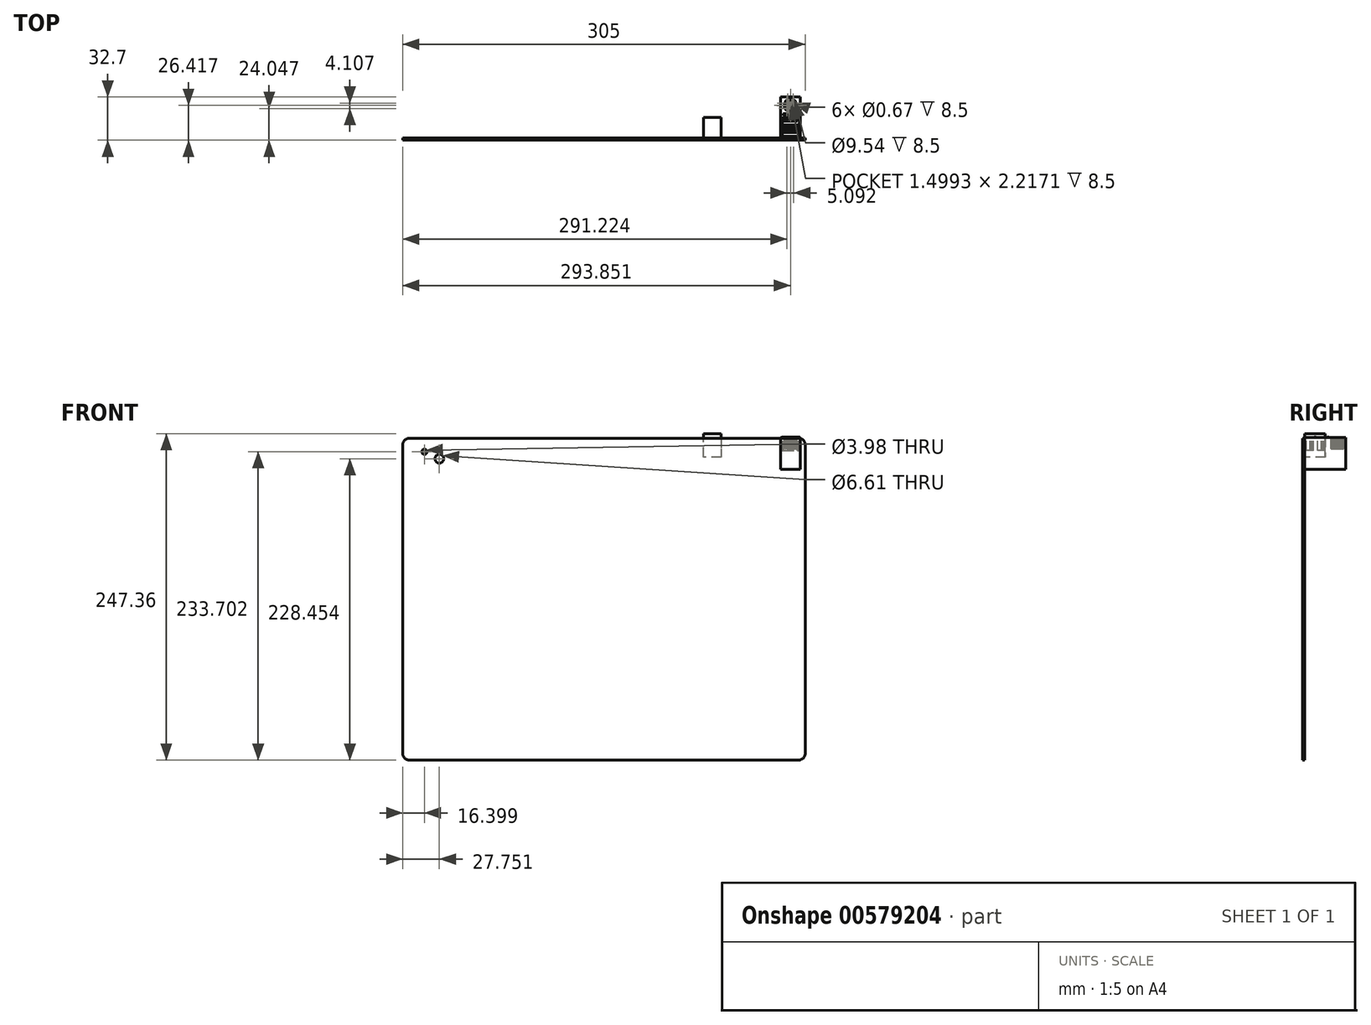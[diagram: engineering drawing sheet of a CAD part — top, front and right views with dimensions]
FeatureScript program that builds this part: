
annotation { "Feature Type Name" : "Feature", "Feature Type Description" : "" }
export const myFeature = defineFeature(function(context is Context, id is Id, definition is map)
    precondition{}
    {
        {
            var Q0;
            Q0=qCreatedBy(makeId("Front.planeOp"),FACE);
            var sketch = newSketch(context, id + "F0", { "sketchPlane" : qUnion([Q0])});
            skPoint(sketch, "E0", {"position": v(-153.4, 107.43) * mm});
            skLineSegment(sketch, "E1", {"start": v(-148.4, 107.43) * mm, "end": v(146.6, 107.43) * mm});
            skPoint(sketch, "E2", {"position": v(151.6, 107.43) * mm});
            skPoint(sketch, "E3", {"position": v(151.6, -136.57) * mm});
            skLineSegment(sketch, "E4", {"start": v(-153.4, 102.43) * mm, "end": v(-153.4, -131.57) * mm});
            skLineSegment(sketch, "E5", {"start": v(-148.4, -136.57) * mm, "end": v(146.6, -136.57) * mm});
            skLineSegment(sketch, "E6", {"start": v(151.6, -131.57) * mm, "end": v(151.6, 102.43) * mm});
            skArc(sketch, "E7.filletArc", {"start": v(-148.4, 107.43) * mm, "mid": v(-151.94, 105.97) * mm, "end": v(-153.4, 102.43) * mm});
            skPoint(sketch, "E8.visualSharp", {"position": v(-153.4, -136.57) * mm});
            skArc(sketch, "E8.filletArc", {"start": v(-153.4, -131.57) * mm, "mid": v(-151.94, -135.1) * mm, "end": v(-148.4, -136.57) * mm});
            skArc(sketch, "E9.filletArc", {"start": v(146.6, -136.57) * mm, "mid": v(150.13, -135.1) * mm, "end": v(151.6, -131.57) * mm});
            skArc(sketch, "E10.filletArc", {"start": v(151.6, 102.43) * mm, "mid": v(150.13, 105.97) * mm, "end": v(146.6, 107.43) * mm});
            skCircle(sketch, "E11", {"center": v(-137, 97.13) * mm, "radius": 1.99 * mm});
            skCircle(sketch, "E12", {"center": v(-125.65, 91.88) * mm, "radius": 3.3 * mm});
            skLineSegment(sketch, "E13.bottom", {"start": v(148.03, 83.7) * mm, "end": v(133.05, 83.7) * mm});
            skLineSegment(sketch, "E13.top", {"start": v(148.03, 108) * mm, "end": v(133.05, 108) * mm});
            skLineSegment(sketch, "E13.left", {"start": v(148.03, 83.7) * mm, "end": v(148.03, 108) * mm});
            skLineSegment(sketch, "E13.right", {"start": v(133.05, 83.7) * mm, "end": v(133.05, 108) * mm});
            skSolve(sketch);
        }
        {
            var Q0;
            {var subQ0=sQuery(id+"F0.wireOp",EDGE,"E13.bottom");Q0=makeQuery(id+"F0.imprint","IMPRINT",FACE,{"disambiguationData":[TD([[makeQuery(id+"F0.imprint","IMPRINT",EDGE,{"derivedFrom":subQ0}),-1.0]])]});}
            var Q1;
            {var subQ1=sQuery(id+"F0.wireOp",EDGE,"E13.top");Q1=makeQuery(id+"F0.imprint","IMPRINT",FACE,{"disambiguationData":[TD([[makeQuery(id+"F0.imprint","IMPRINT",EDGE,{"derivedFrom":subQ1}),1.0]])]});}
            extrude(context, id + "F1", {"entities" : qUnion([Q0, Q1]), "oppositeDirection" : true, "depth" : 31.1 * mm, "offsetDistance" : 25 * mm});
        }
        {
            var Q0;
            Q0=makeQuery(id+"F1.opExtrude","SWEPT_FACE",FACE,{"disambiguationData":[OSD([sQuery(id+"F0.wireOp",EDGE,"E13.top")])]});
            var sketch = newSketch(context, id + "F2", { "sketchPlane" : qUnion([Q0])});
            skCircle(sketch, "E14", {"center": v(140.45, 24.82) * mm, "radius": 4.1 * mm});
            skPoint(sketch, "E14.first.point", {"position": v(137.53, 27.7) * mm});
            skPoint(sketch, "E14.second.point", {"position": v(143.22, 21.78) * mm});
            skPoint(sketch, "E14.third.point", {"position": v(139.8, 20.76) * mm});
            skCircle(sketch, "E15", {"center": v(138.27, 26.54) * mm, "radius": 0.34 * mm});
            skPoint(sketch, "E15.first.point", {"position": v(138.08, 26.81) * mm});
            skPoint(sketch, "E15.second.point", {"position": v(138.5, 26.29) * mm});
            skPoint(sketch, "E15.third.point", {"position": v(138.28, 26.2) * mm});
            skCircle(sketch, "E16", {"center": v(137.82, 24.54) * mm, "radius": 0.34 * mm});
            skPoint(sketch, "E16.first.point", {"position": v(137.63, 24.82) * mm});
            skPoint(sketch, "E16.second.point", {"position": v(138, 24.26) * mm});
            skPoint(sketch, "E16.third.point", {"position": v(137.6, 24.3) * mm});
            skCircle(sketch, "E17", {"center": v(139.37, 22.5) * mm, "radius": 0.34 * mm});
            skPoint(sketch, "E17.first.point", {"position": v(139.18, 22.77) * mm});
            skPoint(sketch, "E17.second.point", {"position": v(139.53, 22.2) * mm});
            skPoint(sketch, "E17.third.point", {"position": v(139.14, 22.25) * mm});
            skCircle(sketch, "E18", {"center": v(141.47, 22.45) * mm, "radius": 0.34 * mm});
            skPoint(sketch, "E18.first.point", {"position": v(141.4, 22.77) * mm});
            skPoint(sketch, "E18.second.point", {"position": v(141.63, 22.15) * mm});
            skPoint(sketch, "E18.third.point", {"position": v(141.27, 22.18) * mm});
            skCircle(sketch, "E19", {"center": v(142.92, 24.6) * mm, "radius": 0.34 * mm});
            skPoint(sketch, "E19.first.point", {"position": v(142.96, 24.93) * mm});
            skPoint(sketch, "E19.second.point", {"position": v(142.93, 24.26) * mm});
            skPoint(sketch, "E19.third.point", {"position": v(143.18, 24.39) * mm});
            skCircle(sketch, "E20", {"center": v(142.39, 26.55) * mm, "radius": 0.33 * mm});
            skPoint(sketch, "E20.first.point", {"position": v(142.43, 26.89) * mm});
            skPoint(sketch, "E20.second.point", {"position": v(142.37, 26.22) * mm});
            skPoint(sketch, "E20.third.point", {"position": v(142.06, 26.6) * mm});
            skLineSegment(sketch, "E21", {"start": v(137.71, 21.75) * mm, "end": v(137.71, 23.04) * mm});
            skLineSegment(sketch, "E22", {"start": v(137.71, 23.04) * mm, "end": v(136.75, 23.04) * mm});
            skLineSegment(sketch, "E23", {"start": v(143.14, 21.71) * mm, "end": v(143.14, 23) * mm});
            skLineSegment(sketch, "E24", {"start": v(143.14, 23) * mm, "end": v(144.14, 23) * mm});
            skLineSegment(sketch, "E25", {"start": v(141.19, 24.96) * mm, "end": v(139.69, 24.96) * mm});
            skLineSegment(sketch, "E26", {"start": v(139.69, 24.96) * mm, "end": v(139.69, 27.18) * mm});
            skLineSegment(sketch, "E27", {"start": v(139.69, 27.18) * mm, "end": v(141.19, 27.18) * mm});
            skLineSegment(sketch, "E28", {"start": v(141.19, 27.18) * mm, "end": v(141.19, 24.96) * mm});
            skLineSegment(sketch, "E29", {"start": v(139.57, 28.83) * mm, "end": v(139.57, 28.1) * mm});
            skLineSegment(sketch, "E30", {"start": v(139.57, 28.1) * mm, "end": v(141.03, 28.1) * mm});
            skLineSegment(sketch, "E31", {"start": v(141.03, 28.1) * mm, "end": v(141.03, 28.88) * mm});
            skCircle(sketch, "E32", {"center": v(140.45, 24.82) * mm, "radius": 4.77 * mm});
            skLineSegment(sketch, "E33.bottom", {"start": v(134.19, 15.25) * mm, "end": v(147.2, 15.25) * mm});
            skLineSegment(sketch, "E33.top", {"start": v(134.19, 9.88) * mm, "end": v(147.2, 9.88) * mm});
            skLineSegment(sketch, "E33.left", {"start": v(134.19, 15.25) * mm, "end": v(134.19, 9.88) * mm});
            skLineSegment(sketch, "E33.right", {"start": v(147.2, 15.25) * mm, "end": v(147.2, 9.88) * mm});
            skLineSegment(sketch, "E34.bottom", {"start": v(135.57, 14.06) * mm, "end": v(145.58, 14.06) * mm});
            skLineSegment(sketch, "E34.top", {"start": v(135.57, 12.8) * mm, "end": v(145.58, 12.8) * mm});
            skLineSegment(sketch, "E34.left", {"start": v(135.57, 14.06) * mm, "end": v(135.57, 12.8) * mm});
            skLineSegment(sketch, "E34.right", {"start": v(145.58, 14.06) * mm, "end": v(145.58, 12.8) * mm});
            skLineSegment(sketch, "E35.bottom", {"start": v(134.53, 8.65) * mm, "end": v(147.03, 8.65) * mm});
            skLineSegment(sketch, "E35.top", {"start": v(134.53, 7.53) * mm, "end": v(147.03, 7.53) * mm});
            skLineSegment(sketch, "E35.left", {"start": v(133.97, 8.1) * mm, "end": v(133.97, 8.1) * mm});
            skLineSegment(sketch, "E35.right", {"start": v(147.6, 8.1) * mm, "end": v(147.6, 8.1) * mm});
            skLineSegment(sketch, "E36.bottom", {"start": v(134.38, 6.68) * mm, "end": v(147.25, 6.68) * mm});
            skLineSegment(sketch, "E36.top", {"start": v(134.38, 1.3) * mm, "end": v(147.25, 1.3) * mm});
            skLineSegment(sketch, "E36.left", {"start": v(134.38, 6.68) * mm, "end": v(134.38, 1.3) * mm});
            skLineSegment(sketch, "E36.right", {"start": v(147.25, 6.68) * mm, "end": v(147.25, 1.3) * mm});
            skLineSegment(sketch, "E37.bottom", {"start": v(135.47, 5.48) * mm, "end": v(145.92, 5.48) * mm});
            skLineSegment(sketch, "E37.top", {"start": v(135.47, 4.14) * mm, "end": v(145.92, 4.14) * mm});
            skLineSegment(sketch, "E37.left", {"start": v(135.47, 5.48) * mm, "end": v(135.47, 4.14) * mm});
            skLineSegment(sketch, "E37.right", {"start": v(145.92, 5.48) * mm, "end": v(145.92, 4.14) * mm});
            skPoint(sketch, "E38.visualSharp", {"position": v(133.97, 8.65) * mm});
            skArc(sketch, "E38.filletArc", {"start": v(134.53, 8.65) * mm, "mid": v(134.13, 8.49) * mm, "end": v(133.97, 8.1) * mm});
            skPoint(sketch, "E39.visualSharp", {"position": v(133.97, 7.53) * mm});
            skArc(sketch, "E39.filletArc", {"start": v(133.97, 8.1) * mm, "mid": v(134.13, 7.7) * mm, "end": v(134.53, 7.53) * mm});
            skPoint(sketch, "E40.visualSharp", {"position": v(147.6, 8.65) * mm});
            skArc(sketch, "E40.filletArc", {"start": v(147.6, 8.1) * mm, "mid": v(147.43, 8.49) * mm, "end": v(147.03, 8.65) * mm});
            skPoint(sketch, "E41.visualSharp", {"position": v(147.6, 7.53) * mm});
            skArc(sketch, "E41.filletArc", {"start": v(147.03, 7.53) * mm, "mid": v(147.43, 7.7) * mm, "end": v(147.6, 8.1) * mm});
            skLineSegment(sketch, "E42.bottom", {"start": v(134.9, 18.4) * mm, "end": v(139.04, 18.4) * mm});
            skLineSegment(sketch, "E42.top", {"start": v(134.9, 17.27) * mm, "end": v(139.04, 17.27) * mm});
            skLineSegment(sketch, "E42.left", {"start": v(134.9, 18.4) * mm, "end": v(134.9, 17.27) * mm});
            skLineSegment(sketch, "E42.right", {"start": v(139.6, 17.83) * mm, "end": v(139.6, 17.83) * mm});
            skLineSegment(sketch, "E43.bottom", {"start": v(146.37, 18.47) * mm, "end": v(142.2, 18.47) * mm});
            skLineSegment(sketch, "E43.top", {"start": v(146.37, 17.35) * mm, "end": v(142.2, 17.35) * mm});
            skLineSegment(sketch, "E43.left", {"start": v(146.37, 18.47) * mm, "end": v(146.37, 17.35) * mm});
            skLineSegment(sketch, "E43.right", {"start": v(141.63, 17.9) * mm, "end": v(141.63, 17.9) * mm});
            skPoint(sketch, "E44.visualSharp", {"position": v(139.6, 18.4) * mm});
            skArc(sketch, "E44.filletArc", {"start": v(139.6, 17.83) * mm, "mid": v(139.44, 18.23) * mm, "end": v(139.04, 18.4) * mm});
            skPoint(sketch, "E45.visualSharp", {"position": v(139.6, 17.27) * mm});
            skArc(sketch, "E45.filletArc", {"start": v(139.04, 17.27) * mm, "mid": v(139.44, 17.43) * mm, "end": v(139.6, 17.83) * mm});
            skPoint(sketch, "E46.visualSharp", {"position": v(141.63, 18.47) * mm});
            skArc(sketch, "E46.filletArc", {"start": v(142.2, 18.47) * mm, "mid": v(141.8, 18.3) * mm, "end": v(141.63, 17.9) * mm});
            skPoint(sketch, "E47.visualSharp", {"position": v(141.63, 17.35) * mm});
            skArc(sketch, "E47.filletArc", {"start": v(141.63, 17.9) * mm, "mid": v(141.8, 17.51) * mm, "end": v(142.2, 17.35) * mm});
            skSolve(sketch);
        }
        {
            var Q0;
            {var subQ0=sQuery(id+"F2.wireOp",EDGE,"E21");Q0=makeQuery(id+"F2.imprint","IMPRINT",FACE,{"disambiguationData":[TD([[makeQuery(id+"F2.imprint","IMPRINT",EDGE,{"derivedFrom":subQ0}),1.0]])]});}
            var Q1;
            Q1=makeQuery(id+"F2.imprint","IMPRINT",FACE,{"disambiguationData":[TD([[makeQuery(id+"F2.imprint","IMPRINT",EDGE,{"derivedFrom":sQuery(id+"F2.wireOp",EDGE,"E32")}),1.0]])]});
            var Q2;
            {var subQ0=sQuery(id+"F2.wireOp",EDGE,"E23");Q2=makeQuery(id+"F2.imprint","IMPRINT",FACE,{"disambiguationData":[TD([[makeQuery(id+"F2.imprint","IMPRINT",EDGE,{"derivedFrom":subQ0}),-1.0]])]});}
            var Q3;
            Q3=makeQuery(id+"F2.imprint","IMPRINT",FACE,{"disambiguationData":[TD([[makeQuery(id+"F2.imprint","IMPRINT",EDGE,{"derivedFrom":sQuery(id+"F2.wireOp",EDGE,"E18")}),1.0]])]});
            var Q4;
            Q4=makeQuery(id+"F2.imprint","IMPRINT",FACE,{"disambiguationData":[TD([[makeQuery(id+"F2.imprint","IMPRINT",EDGE,{"derivedFrom":sQuery(id+"F2.wireOp",EDGE,"E17")}),1.0]])]});
            var Q5;
            Q5=makeQuery(id+"F2.imprint","IMPRINT",FACE,{"disambiguationData":[TD([[makeQuery(id+"F2.imprint","IMPRINT",EDGE,{"derivedFrom":sQuery(id+"F2.wireOp",EDGE,"E16")}),1.0]])]});
            var Q6;
            Q6=makeQuery(id+"F2.imprint","IMPRINT",FACE,{"disambiguationData":[TD([[makeQuery(id+"F2.imprint","IMPRINT",EDGE,{"derivedFrom":sQuery(id+"F2.wireOp",EDGE,"E15")}),1.0]])]});
            var Q7;
            Q7=makeQuery(id+"F2.imprint","IMPRINT",FACE,{"disambiguationData":[TD([[makeQuery(id+"F2.imprint","IMPRINT",EDGE,{"derivedFrom":sQuery(id+"F2.wireOp",EDGE,"E25")}),-1.0]])]});
            var Q8;
            Q8=makeQuery(id+"F2.imprint","IMPRINT",FACE,{"disambiguationData":[TD([[makeQuery(id+"F2.imprint","IMPRINT",EDGE,{"derivedFrom":sQuery(id+"F2.wireOp",EDGE,"E20")}),1.0]])]});
            var Q9;
            Q9=makeQuery(id+"F2.imprint","IMPRINT",FACE,{"disambiguationData":[TD([[makeQuery(id+"F2.imprint","IMPRINT",EDGE,{"derivedFrom":sQuery(id+"F2.wireOp",EDGE,"E19")}),1.0]])]});
            var Q10;
            {var subQ0=sQuery(id+"F2.wireOp",EDGE,"E29");Q10=makeQuery(id+"F2.imprint","IMPRINT",FACE,{"disambiguationData":[TD([[makeQuery(id+"F2.imprint","IMPRINT",EDGE,{"derivedFrom":subQ0}),1.0]])]});}
            extrude(context, id + "F3", {"entities" : qUnion([Q0, Q1, Q2, Q3, Q4, Q5, Q6, Q7, Q8, Q9, Q10]), "operationType" : NewBodyOperationType.REMOVE, "oppositeDirection" : true, "depth" : 8.5 * mm, "offsetDistance" : 25 * mm});
        }
        {
            var Q0;
            Q0=makeQuery(id+"F2.imprint","IMPRINT",FACE,{"disambiguationData":[TD([[makeQuery(id+"F2.imprint","IMPRINT",EDGE,{"derivedFrom":sQuery(id+"F2.wireOp",EDGE,"E42.bottom")}),-1.0]])]});
            var Q1;
            Q1=makeQuery(id+"F2.imprint","IMPRINT",FACE,{"disambiguationData":[TD([[makeQuery(id+"F2.imprint","IMPRINT",EDGE,{"derivedFrom":sQuery(id+"F2.wireOp",EDGE,"E43.bottom")}),1.0]])]});
            extrude(context, id + "F4", {"entities" : qUnion([Q0, Q1]), "operationType" : NewBodyOperationType.ADD, "depth" : .3 * mm, "offsetDistance" : 25 * mm});
        }
        {
            var Q0;
            Q0=makeQuery(id+"F2.imprint","IMPRINT",FACE,{"disambiguationData":[TD([[makeQuery(id+"F2.imprint","IMPRINT",EDGE,{"derivedFrom":sQuery(id+"F2.wireOp",EDGE,"E33.bottom")}),-1.0]])]});
            var Q1;
            Q1=makeQuery(id+"F2.imprint","IMPRINT",FACE,{"disambiguationData":[TD([[makeQuery(id+"F2.imprint","IMPRINT",EDGE,{"derivedFrom":sQuery(id+"F2.wireOp",EDGE,"E36.bottom")}),-1.0]])]});
            extrude(context, id + "F5", {"entities" : qUnion([Q0, Q1]), "operationType" : NewBodyOperationType.REMOVE, "oppositeDirection" : true, "depth" : 10 * mm, "offsetDistance" : 25 * mm});
        }
        {
            var Q0;
            Q0=makeQuery(id+"F2.imprint","IMPRINT",FACE,{"disambiguationData":[TD([[makeQuery(id+"F2.imprint","IMPRINT",EDGE,{"derivedFrom":sQuery(id+"F2.wireOp",EDGE,"E35.bottom")}),-1.0]])]});
            extrude(context, id + "F6", {"entities" : qUnion([Q0]), "operationType" : NewBodyOperationType.ADD, "depth" : .3 * mm, "offsetDistance" : 25 * mm});
        }
        {
            var Q0;
            Q0=makeQuery(id+"F0.imprint","IMPRINT",FACE,{"disambiguationData":[TD([[makeQuery(id+"F0.imprint","IMPRINT",EDGE,{"derivedFrom":sQuery(id+"F0.wireOp",EDGE,"E4")}),1.0]])]});
            extrude(context, id + "F7", {"entities" : qUnion([Q0]), "depth" : 1.6 * mm, "offsetDistance" : 25 * mm});
        }
        {
            var Q0;
            {var subQ0=sQuery(id+"F0.wireOp",EDGE,"E13.bottom");Q0=makeQuery(id+"F0.imprint","IMPRINT",FACE,{"disambiguationData":[TD([[makeQuery(id+"F0.imprint","IMPRINT",EDGE,{"derivedFrom":subQ0}),-1.0]])]});}
            extrude(context, id + "F8", {"entities" : qUnion([Q0]), "depth" : 1.6 * mm, "offsetDistance" : 25 * mm});
        }
        {
            var Q0;
            Q0=makeQuery(id+"F0.imprint","IMPRINT",FACE,{"disambiguationData":[TD([[makeQuery(id+"F0.imprint","IMPRINT",EDGE,{"derivedFrom":sQuery(id+"F0.wireOp",EDGE,"E4")}),1.0]])]});
            var sketch = newSketch(context, id + "F9", { "sketchPlane" : qUnion([Q0])});
            skLineSegment(sketch, "E48", {"start": v(87.94, 110.8) * mm, "end": v(87.94, 93) * mm});
            skLineSegment(sketch, "E49", {"start": v(87.94, 93) * mm, "end": v(74.51, 93) * mm});
            skLineSegment(sketch, "E50", {"start": v(74.51, 93) * mm, "end": v(74.51, 110.67) * mm});
            skLineSegment(sketch, "E51", {"start": v(74.51, 110.67) * mm, "end": v(87.94, 110.8) * mm});
            skSolve(sketch);
        }
        {
            var Q0;
            {var subQ0=sQuery(id+"F9.wireOp",EDGE,"E51");Q0=makeQuery(id+"F9.imprint","IMPRINT",FACE,{"disambiguationData":[TD([[makeQuery(id+"F9.imprint","IMPRINT",EDGE,{"derivedFrom":subQ0}),-1.0]])]});}
            var Q1;
            {var subQ0=sQuery(id+"F9.wireOp",EDGE,"E49");Q1=makeQuery(id+"F9.imprint","IMPRINT",FACE,{"disambiguationData":[TD([[makeQuery(id+"F9.imprint","IMPRINT",EDGE,{"derivedFrom":subQ0}),-1.0]])]});}
            extrude(context, id + "F10", {"entities" : qUnion([Q0, Q1]), "operationType" : NewBodyOperationType.ADD, "oppositeDirection" : true, "depth" : 15.6 * mm, "offsetDistance" : 25 * mm});
        }
    });
